# Revit family: Nuaire_IfcFanType_Cyfan
name_source: partatom
category: Mechanical Equipment
revit_build: Autodesk Revit 2018 (Build: 20170223_1515(x64)
units: mm (PartAtom-declared; Revit-internal decimal feet)

## family parameters
Always vertical = Yes
Cut with Voids When Loaded = No
OmniClass Number = 23.75.00.00
OmniClass Title = Climate Control (HVAC)
Part Type = Normal
Room Calculation Point = No
Round Connector Dimension = Use Radius
Shared = No
Work Plane-Based = No

## types (1)
- CYFAN
    6 Monthly = SFG20 20-03
    Annually = SFG20 20-03
    Apparent Load = 67.39 VA
    BMS Links = No
    Battery Supply = No
    COBie.Type = Yes
    COBie.Type.Category = Pr_65_67_29_12 : Centrifugal Fans
    COBie.Type.Description = 230V/24V DC SELV Surface and Semi-Recess Mounted Fan
    COBie.Type.Length = 137 mm
    COBie.Type.Manufacturer = Nuaire
    COBie.Type.ModelNumber = CYFAN
    COBie.Type.Name = CYFAN
    COBie.Type.NominalHeight = 208 mm
    COBie.Type.NominalLength = 137 mm
    COBie.Type.NominalWidth = 207 mm
    COBie.Type.ReplacementCost = 0 $
    COBie.Type.WarrantyDescription = First year parts and labour, remaining 4 years parts only.
    COBie.Type.WarrantyDurationLabor = 1
    COBie.Type.WarrantyDurationParts = 5
    COBie.Type.WarrantyDurationUnit = Year
    COBie.Type.WarrantyGuarantorLabor = Nuaire
    COBie.Type.WarrantyGuarantorParts = Nuaire
    Catalogue Pages = http://nuaire.info
    Classification System = Uniclass2015
    Classification.Uniclass.Pr.Description = Centrifugal Fans
    Classification.Uniclass.Pr.Number = Pr_65_67_29_12
    Daily = SFG20 20-03
    Description = 230V/24V DC SELV Surface and Semi-Recess Mounted Fan
    Environmental Product Declaration = WEEE, RoHS
    Fan Unit = Yes
    Fax Number = +44(0)2920-858-222
    Fire Control Panel Links = No
    Frequency = 50 Hz
    Full Load Current = 0.293 A
    Height = 208 mm
    I&M Manual = http://nuaire.info
    IFCExportAs = IfcFanType
    IFCExportType = CENTRIFUGALFORWARDCURVED
    Length = 137 mm
    Life Cycle Analysis = 0
    Location of Manufacturer = 51.571856, -3.232638
    Maintenance Required 0 to 300hrs = http://nuaire.info
    Maintenance Required 1001 to 2000hrs = http://nuaire.info
    Maintenance Required 2001 to 4000hrs = http://nuaire.info
    Maintenance Required 301 to 600hrs = http://nuaire.info
    Maintenance Required 4001 to 8000hrs = http://nuaire.info
    Maintenance Required 601 to 1000hrs = http://nuaire.info
    Maintenance Required 8001 to 12000hrs = http://nuaire.info
    Manufacturer = Nuaire
    Manufacturer Name = Nuaire
    Maximum Ambient Temperature = 40.00 °C
    Model = CYFAN
    Monthly = SFG20 20-03
    Nominal Motor Rating = 0.033 kW
    Nominal Motor Speed (rpm) = 2500
    Nuaire Model Code = CYFAN
    Number of Connection Poles = 2
    OmniClass Number = 23-33 31 19 13
    OmniClass Title = Centrifugal Fans
    Operation and Maintenance Manual = http://nuaire.info
    Postcode = CF83 1NA
    Power Source = Mains
    Product Literature = http://nuaire.info
    Product Range = Cyfan
    Quarterly = SFG20 20-03
    Reference Standard = BS EN 60335-2-80
    Responsible Sourcing of Materials = FSC
    Revit Family Last Revised = 2020-09-23T12:21:00
    Starting Current = 1.000 A
    Suitability for Use = Approved
    Supply Phase = 1
    Telephone Number = +44(0)2920-858-200
    Template Custodian = Nuaire
    URL = http://www.nuaire.co.uk
    VAT Registration Number = 877308
    Voltage = 230.00 V
    Warranty Period = 5 Years
    Weatherproof or Internal Only = Internal
    Weekly = SFG20 20-03
    Weight = 1.40 kg
    Width = 207 mm

## geometry (parser evidence)
native form markers: Blend x32, Sweep x13
no freeform markers — native parametric forms only
